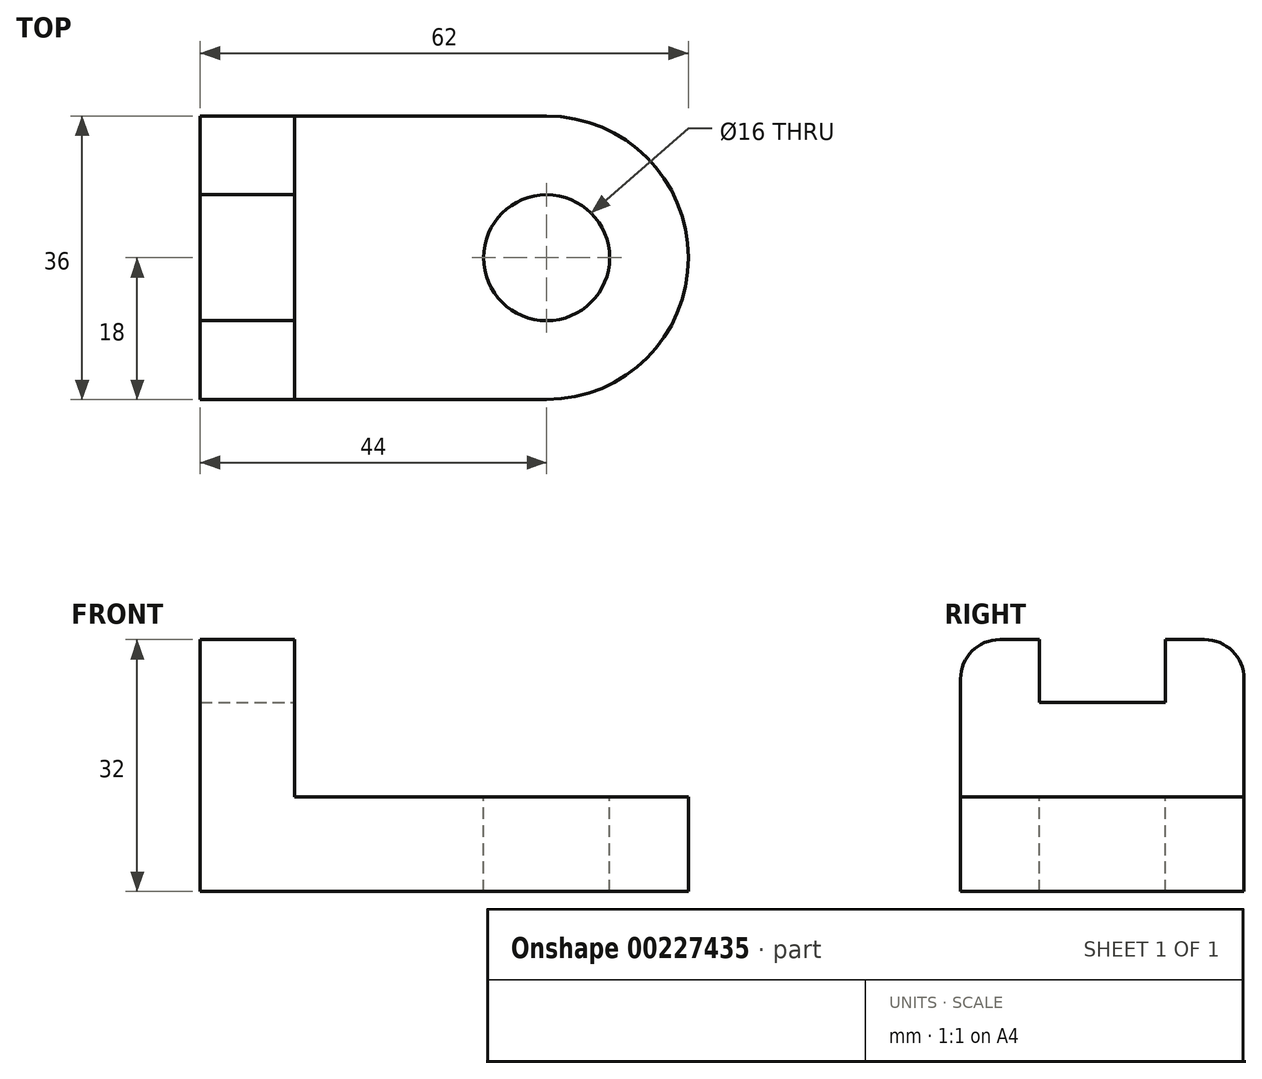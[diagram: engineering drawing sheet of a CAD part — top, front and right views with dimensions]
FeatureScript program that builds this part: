
annotation { "Feature Type Name" : "Feature", "Feature Type Description" : "" }
export const myFeature = defineFeature(function(context is Context, id is Id, definition is map)
    precondition{}
    {
        {
            var Q0;
            Q0=qCreatedBy(makeId("Top.planeOp"),FACE);
            var sketch = newSketch(context, id + "F0", { "sketchPlane" : qUnion([Q0])});
            skLineSegment(sketch, "E0.bottom", {"start": v(-44, 18) * mm, "end": v(18, 18) * mm});
            skLineSegment(sketch, "E0.top", {"start": v(-44, -18) * mm, "end": v(18, -18) * mm});
            skLineSegment(sketch, "E0.left", {"start": v(-44, 18) * mm, "end": v(-44, -18) * mm});
            skLineSegment(sketch, "E0.right", {"start": v(18, 18) * mm, "end": v(18, -18) * mm});
            skSolve(sketch);
        }
        {
            var Q0;
            Q0 = qSketchRegion(id + "F0", true);
            extrude(context, id + "F1", {"entities" : qUnion([Q0]), "depth" : 32 * mm});
        }
        {
            var Q0;
            Q0=makeQuery(id+"F1.opExtrude","SWEPT_FACE",FACE,{"disambiguationData":[OSD([sQuery(id+"F0.wireOp",EDGE,"E0.top")])]});
            var sketch = newSketch(context, id + "F2", { "sketchPlane" : qUnion([Q0])});
            skLineSegment(sketch, "E1.bottom", {"start": v(-32, 42) * mm, "end": v(28, 42) * mm});
            skLineSegment(sketch, "E1.top", {"start": v(-32, 12) * mm, "end": v(28, 12) * mm});
            skLineSegment(sketch, "E1.left", {"start": v(-32, 42) * mm, "end": v(-32, 12) * mm});
            skLineSegment(sketch, "E1.right", {"start": v(28, 42) * mm, "end": v(28, 12) * mm});
            skSolve(sketch);
        }
        {
            var Q0;
            Q0 = qSketchRegion(id + "F2", true);
            extrude(context, id + "F3", {"entities" : qUnion([Q0]), "operationType" : NewBodyOperationType.REMOVE, "endBound" : BoundingType.THROUGH_ALL, "oppositeDirection" : true, "depth" : 29.36 * mm});
        }
        {
            var Q0;
            Q0=makeQuery(id+"F3.boolean.opBoolean","COPY",FACE,{"derivedFrom":makeQuery(id+"F3.opExtrude","SWEPT_FACE",FACE,{"disambiguationData":[OSD([sQuery(id+"F2.wireOp",EDGE,"E1.top")])]})});
            var sketch = newSketch(context, id + "F4", { "sketchPlane" : qUnion([Q0])});
            skArc(sketch, "E2", {"start": v(0, -18) * mm, "mid": v(18, 0) * mm, "end": v(0, 18) * mm});
            skLineSegment(sketch, "E3", {"start": v(0, 28) * mm, "end": v(28, 28) * mm});
            skLineSegment(sketch, "E4", {"start": v(28, 28) * mm, "end": v(28, -28) * mm});
            skLineSegment(sketch, "E5", {"start": v(28, -28) * mm, "end": v(0, -28) * mm});
            skLineSegment(sketch, "E6", {"start": v(0, -28) * mm, "end": v(0, -18) * mm});
            skLineSegment(sketch, "E7", {"start": v(0, 28) * mm, "end": v(0, 18) * mm});
            skSolve(sketch);
        }
        {
            var Q0;
            Q0 = qSketchRegion(id + "F4", true);
            extrude(context, id + "F5", {"entities" : qUnion([Q0]), "operationType" : NewBodyOperationType.REMOVE, "endBound" : BoundingType.THROUGH_ALL, "oppositeDirection" : true, "depth" : 13.6 * mm});
        }
        {
            var Q0;
            Q0=makeQuery(id+"F3.boolean.opBoolean","COPY",FACE,{"derivedFrom":makeQuery(id+"F3.opExtrude","SWEPT_FACE",FACE,{"disambiguationData":[OSD([sQuery(id+"F2.wireOp",EDGE,"E1.left")])]})});
            var sketch = newSketch(context, id + "F6", { "sketchPlane" : qUnion([Q0])});
            skLineSegment(sketch, "E8.bottom", {"start": v(-8, 36) * mm, "end": v(8, 36) * mm});
            skLineSegment(sketch, "E8.top", {"start": v(-8, 24) * mm, "end": v(8, 24) * mm});
            skLineSegment(sketch, "E8.left", {"start": v(-8, 36) * mm, "end": v(-8, 24) * mm});
            skLineSegment(sketch, "E8.right", {"start": v(8, 36) * mm, "end": v(8, 24) * mm});
            skSolve(sketch);
        }
        {
            var Q0;
            Q0 = qSketchRegion(id + "F6", true);
            extrude(context, id + "F7", {"entities" : qUnion([Q0]), "operationType" : NewBodyOperationType.REMOVE, "endBound" : BoundingType.THROUGH_ALL, "oppositeDirection" : true, "depth" : 22.04 * mm});
        }
        {
            var Q0;
            Q0=makeQuery(id+"F3.boolean.opBoolean","COPY",FACE,{"derivedFrom":makeQuery(id+"F3.opExtrude","SWEPT_FACE",FACE,{"disambiguationData":[OSD([sQuery(id+"F2.wireOp",EDGE,"E1.top")])]})});
            var sketch = newSketch(context, id + "F8", { "sketchPlane" : qUnion([Q0])});
            skCircle(sketch, "E9", {"center": v(0, 0) * mm, "radius": 8 * mm});
            skSolve(sketch);
        }
        {
            var Q0;
            Q0 = qSketchRegion(id + "F8", true);
            extrude(context, id + "F9", {"entities" : qUnion([Q0]), "operationType" : NewBodyOperationType.REMOVE, "endBound" : BoundingType.THROUGH_ALL, "oppositeDirection" : true, "depth" : 22.58 * mm});
        }
        {
            var Q0;
            Q0=makeQuery(id+"F1.opExtrude","CAP_EDGE",EDGE,{"disambiguationData":[OSD([sQuery(id+"F0.wireOp",EDGE,"E0.bottom")])],"isStart":false});
            var Q1;
            Q1=makeQuery(id+"F1.opExtrude","CAP_EDGE",EDGE,{"disambiguationData":[OSD([sQuery(id+"F0.wireOp",EDGE,"E0.top")])],"isStart":false});
            fillet(context, id + "F10", {"entities" : qUnion([Q0, Q1]), "radius" : 5 * mm, "tangentPropagation" : true, "allowEdgeOverflow" : false});
        }
    });
